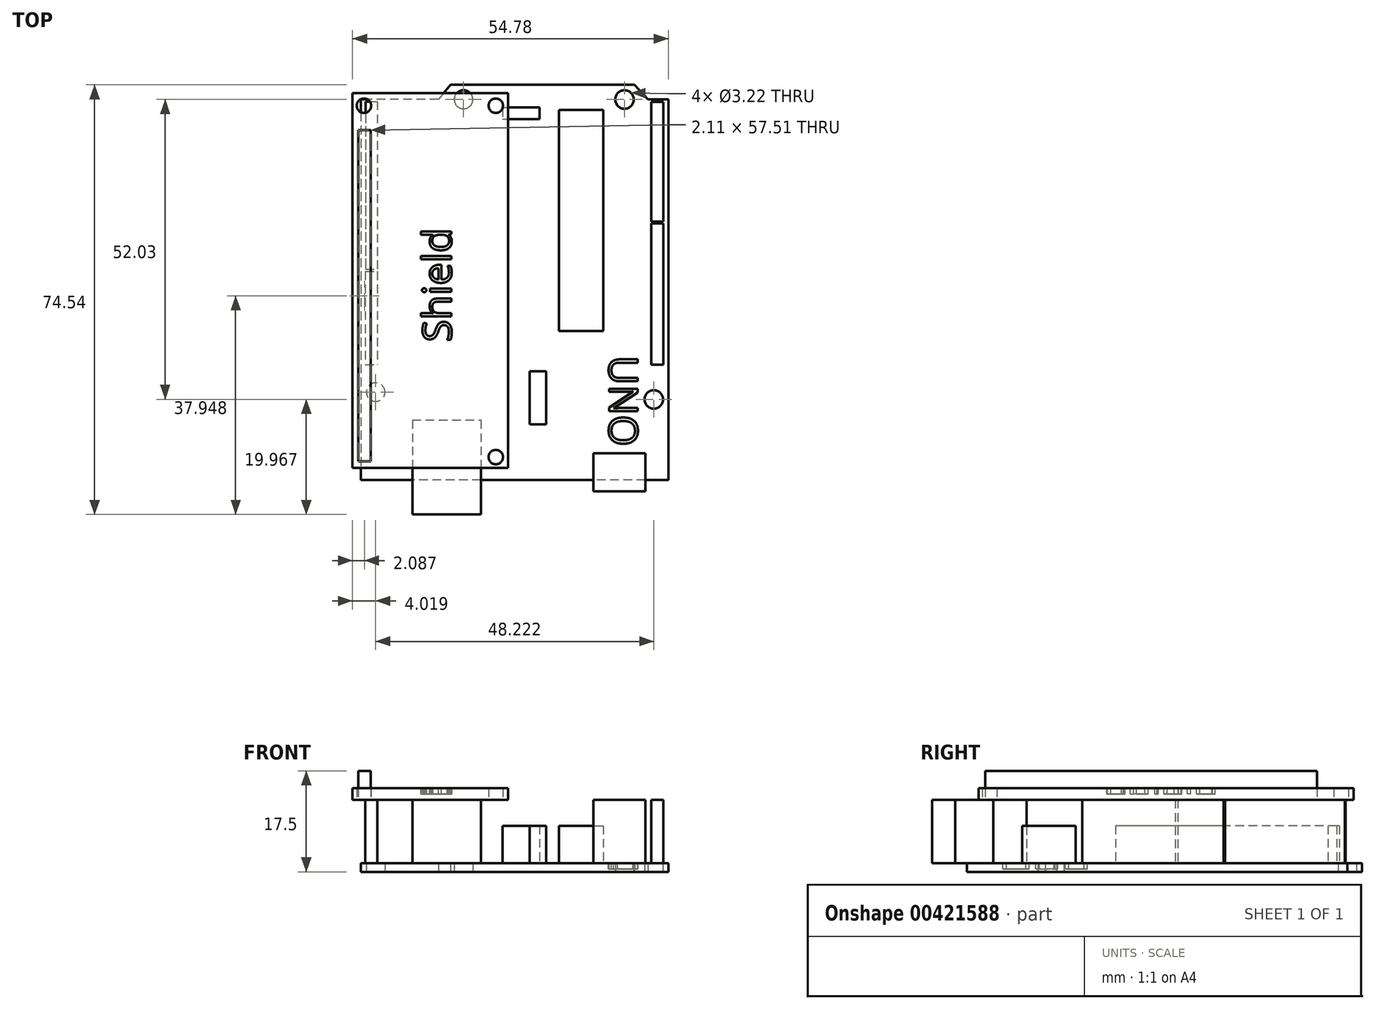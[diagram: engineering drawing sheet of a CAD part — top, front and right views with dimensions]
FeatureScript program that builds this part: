
annotation { "Feature Type Name" : "Feature", "Feature Type Description" : "" }
export const myFeature = defineFeature(function(context is Context, id is Id, definition is map)
    precondition{}
    {
        {
            var Q0;
            Q0=qCreatedBy(makeId("Top.planeOp"),FACE);
            var sketch = newSketch(context, id + "F0", { "sketchPlane" : qUnion([Q0])});
            skLineSegment(sketch, "E0.bottom", {"start": v(26.65, 33) * mm, "end": v(-26.65, 33) * mm});
            skLineSegment(sketch, "E0.top", {"start": v(26.65, -33) * mm, "end": v(-26.65, -33) * mm});
            skLineSegment(sketch, "E0.left", {"start": v(26.65, 33) * mm, "end": v(26.65, -33) * mm});
            skLineSegment(sketch, "E0.right", {"start": v(-26.65, 33) * mm, "end": v(-26.65, -33) * mm});
            skPoint(sketch, "E0.middle", {"position": v(0, 0) * mm});
            skLineSegment(sketch, "E1.bottom", {"start": v(-17.75, -22.62) * mm, "end": v(-5.85, -22.62) * mm});
            skLineSegment(sketch, "E1.top", {"start": v(-17.75, -39) * mm, "end": v(-5.85, -39) * mm});
            skLineSegment(sketch, "E1.left", {"start": v(-17.75, -22.62) * mm, "end": v(-17.75, -39) * mm});
            skLineSegment(sketch, "E1.right", {"start": v(-5.85, -22.62) * mm, "end": v(-5.85, -39) * mm});
            skLineSegment(sketch, "E2.bottom", {"start": v(7.67, 31.17) * mm, "end": v(15.35, 31.17) * mm});
            skLineSegment(sketch, "E2.top", {"start": v(7.67, -7.2) * mm, "end": v(15.35, -7.2) * mm});
            skLineSegment(sketch, "E2.left", {"start": v(7.67, 31.17) * mm, "end": v(7.67, -7.2) * mm});
            skLineSegment(sketch, "E2.right", {"start": v(15.35, 31.17) * mm, "end": v(15.35, -7.2) * mm});
            skLineSegment(sketch, "E3.bottom", {"start": v(2.6, -14.13) * mm, "end": v(5.43, -14.13) * mm});
            skLineSegment(sketch, "E3.top", {"start": v(2.6, -23.39) * mm, "end": v(5.43, -23.39) * mm});
            skLineSegment(sketch, "E3.left", {"start": v(2.6, -14.13) * mm, "end": v(2.6, -23.39) * mm});
            skLineSegment(sketch, "E3.right", {"start": v(5.43, -14.13) * mm, "end": v(5.43, -23.39) * mm});
            skLineSegment(sketch, "E4.bottom", {"start": v(-25.88, 32.67) * mm, "end": v(-23.85, 32.67) * mm});
            skLineSegment(sketch, "E4.top", {"start": v(-25.88, 3.57) * mm, "end": v(-23.85, 3.57) * mm});
            skLineSegment(sketch, "E4.left", {"start": v(-25.88, 32.67) * mm, "end": v(-25.88, 3.57) * mm});
            skLineSegment(sketch, "E4.right", {"start": v(-23.85, 32.67) * mm, "end": v(-23.85, 3.57) * mm});
            skLineSegment(sketch, "E5.bottom", {"start": v(-25.9, 3.18) * mm, "end": v(-23.82, 3.18) * mm});
            skLineSegment(sketch, "E5.top", {"start": v(-25.9, -13) * mm, "end": v(-23.82, -13) * mm});
            skLineSegment(sketch, "E5.left", {"start": v(-25.9, 3.18) * mm, "end": v(-25.9, -13) * mm});
            skLineSegment(sketch, "E5.right", {"start": v(-23.82, 3.18) * mm, "end": v(-23.82, -13) * mm});
            skLineSegment(sketch, "E6.bottom", {"start": v(25.78, 32.58) * mm, "end": v(23.65, 32.58) * mm});
            skLineSegment(sketch, "E6.top", {"start": v(25.78, 11.8) * mm, "end": v(23.65, 11.8) * mm});
            skLineSegment(sketch, "E6.left", {"start": v(23.65, 32.58) * mm, "end": v(23.65, 11.8) * mm});
            skLineSegment(sketch, "E7.bottom", {"start": v(25.75, 11.51) * mm, "end": v(23.66, 11.51) * mm});
            skLineSegment(sketch, "E7.top", {"start": v(25.75, -13) * mm, "end": v(23.66, -13) * mm});
            skLineSegment(sketch, "E7.left", {"start": v(25.75, 11.51) * mm, "end": v(25.75, -13) * mm});
            skLineSegment(sketch, "E7.right", {"start": v(23.66, 11.51) * mm, "end": v(23.66, -13) * mm});
            skLineSegment(sketch, "E8.bottom", {"start": v(-2.12, 31.63) * mm, "end": v(4.28, 31.63) * mm});
            skLineSegment(sketch, "E8.top", {"start": v(-2.12, 29.62) * mm, "end": v(4.28, 29.62) * mm});
            skLineSegment(sketch, "E8.left", {"start": v(-2.12, 31.63) * mm, "end": v(-2.12, 29.62) * mm});
            skLineSegment(sketch, "E8.right", {"start": v(4.28, 31.63) * mm, "end": v(4.28, 29.62) * mm});
            skText(sketch, "E9", { "text": "UNO", "fontName": "OpenSans-Regular.ttf"});
            skCircle(sketch, "E10", {"center": v(19.03, 33) * mm, "radius": 1.6 * mm});
            skCircle(sketch, "E11", {"center": v(-8.88, 33) * mm, "radius": 1.6 * mm});
            skLineSegment(sketch, "E12", {"start": v(-11.15, 35.54) * mm, "end": v(20.74, 35.54) * mm});
            skLineSegment(sketch, "E13", {"start": v(20.74, 35.54) * mm, "end": v(23.07, 33) * mm});
            skCircle(sketch, "E14", {"center": v(24.11, -19.03) * mm, "radius": 1.6 * mm});
            skLineSegment(sketch, "E15", {"start": v(25.78, 11.8) * mm, "end": v(25.78, 32.58) * mm});
            skCircle(sketch, "E16", {"center": v(-24.11, -17.76) * mm, "radius": 1.6 * mm});
            skLineSegment(sketch, "E17", {"start": v(-11.15, 35.54) * mm, "end": v(-13.22, 33) * mm});
            skLineSegment(sketch, "E18", {"start": v(13.65, -28.4) * mm, "end": v(13.65, -35) * mm});
            skLineSegment(sketch, "E19", {"start": v(13.65, -35) * mm, "end": v(22.65, -35) * mm});
            skLineSegment(sketch, "E20", {"start": v(22.65, -35) * mm, "end": v(22.65, -28.4) * mm});
            skLineSegment(sketch, "E21", {"start": v(22.65, -28.4) * mm, "end": v(13.65, -28.4) * mm});
            const initialGuessF0  = {"E9": [0.01473, -0.00947, 0, -1, 0.005]};
            skSetInitialGuess(sketch, initialGuessF0);
            skSolve(sketch);
        }
        {
            var Q0;
            Q0=makeQuery(id+"F0.imprint","IMPRINT",FACE,{"disambiguationData":[TD([[makeQuery(id+"F0.imprint","IMPRINT",EDGE,{"derivedFrom":sQuery(id+"F0.wireOp",EDGE,"E0.bottom")}),1.0]])]});
            var Q1;
            Q1=makeQuery(id+"F0.imprint","IMPRINT",FACE,{"disambiguationData":[TD([[makeQuery(id+"F0.imprint","IMPRINT",EDGE,{"derivedFrom":sQuery(id+"F0.wireOp",EDGE,"E9.sketch_text.stroke-37")}),1.0]])]});
            var Q2;
            Q2=makeQuery(id+"F0.imprint","IMPRINT",FACE,{"disambiguationData":[TD([[makeQuery(id+"F0.imprint","IMPRINT",EDGE,{"derivedFrom":sQuery(id+"F0.wireOp",EDGE,"E9.sketch_text.stroke-0")}),-1.0]])]});
            var Q3;
            Q3=makeQuery(id+"F0.imprint","IMPRINT",FACE,{"disambiguationData":[TD([[makeQuery(id+"F0.imprint","IMPRINT",EDGE,{"derivedFrom":sQuery(id+"F0.wireOp",EDGE,"E9.sketch_text.stroke-14")}),-1.0]])]});
            var Q4;
            Q4=makeQuery(id+"F0.imprint","IMPRINT",FACE,{"disambiguationData":[TD([[makeQuery(id+"F0.imprint","IMPRINT",EDGE,{"derivedFrom":sQuery(id+"F0.wireOp",EDGE,"E9.sketch_text.stroke-29")}),-1.0]])]});
            var Q5;
            Q5=makeQuery(id+"F0.imprint","IMPRINT",FACE,{"disambiguationData":[TD([[makeQuery(id+"F0.imprint","IMPRINT",EDGE,{"derivedFrom":sQuery(id+"F0.wireOp",EDGE,"E12")}),-1.0]])]});
            extrude(context, id + "F1", {"entities" : qUnion([Q0, Q1, Q2, Q3, Q4, Q5]), "depth" : 1.5 * mm, "offsetDistance" : 25 * mm});
        }
        {
            var Q0;
            Q0=makeQuery(id+"F0.imprint","IMPRINT",FACE,{"disambiguationData":[TD([[makeQuery(id+"F0.imprint","IMPRINT",EDGE,{"derivedFrom":sQuery(id+"F0.wireOp",EDGE,"E4.bottom")}),-1.0]])]});
            var Q1;
            Q1=makeQuery(id+"F0.imprint","IMPRINT",FACE,{"disambiguationData":[TD([[makeQuery(id+"F0.imprint","IMPRINT",EDGE,{"derivedFrom":sQuery(id+"F0.wireOp",EDGE,"E6.bottom")}),1.0]])]});
            var Q2;
            Q2=makeQuery(id+"F0.imprint","IMPRINT",FACE,{"disambiguationData":[TD([[makeQuery(id+"F0.imprint","IMPRINT",EDGE,{"derivedFrom":sQuery(id+"F0.wireOp",EDGE,"E7.bottom")}),1.0]])]});
            var Q3;
            Q3=makeQuery(id+"F0.imprint","IMPRINT",FACE,{"disambiguationData":[TD([[makeQuery(id+"F0.imprint","IMPRINT",EDGE,{"derivedFrom":sQuery(id+"F0.wireOp",EDGE,"E5.bottom")}),-1.0]])]});
            var Q4;
            {var subQ5=sQuery(id+"F0.wireOp",EDGE,"E1.top");Q4=makeQuery(id+"F0.imprint","IMPRINT",FACE,{"disambiguationData":[TD([[makeQuery(id+"F0.imprint","IMPRINT",EDGE,{"derivedFrom":subQ5}),1.0]])]});}
            var Q5;
            {var subQ5=sQuery(id+"F0.wireOp",EDGE,"E1.bottom");Q5=makeQuery(id+"F0.imprint","IMPRINT",FACE,{"disambiguationData":[TD([[makeQuery(id+"F0.imprint","IMPRINT",EDGE,{"derivedFrom":subQ5}),-1.0]])]});}
            var Q6;
            {var subQ5=sQuery(id+"F0.wireOp",EDGE,"0UXD3os9-Lv6w-TNBq-ahMY-INUZyBISBa7V.top");Q6=makeQuery(id+"F0.imprint","IMPRINT",FACE,{"disambiguationData":[TD([[makeQuery(id+"F0.imprint","IMPRINT",EDGE,{"derivedFrom":subQ5}),-1.0]])]});}
            var Q7;
            {var subQ5=sQuery(id+"F0.wireOp",EDGE,"0UXD3os9-Lv6w-TNBq-ahMY-INUZyBISBa7V.bottom");Q7=makeQuery(id+"F0.imprint","IMPRINT",FACE,{"disambiguationData":[TD([[makeQuery(id+"F0.imprint","IMPRINT",EDGE,{"derivedFrom":subQ5}),1.0]])]});}
            var Q8;
            {var subQ5=sQuery(id+"F0.wireOp",EDGE,"E21");Q8=makeQuery(id+"F0.imprint","IMPRINT",FACE,{"disambiguationData":[TD([[makeQuery(id+"F0.imprint","IMPRINT",EDGE,{"derivedFrom":subQ5}),1.0]])]});}
            var Q9;
            {var subQ5=sQuery(id+"F0.wireOp",EDGE,"E19");Q9=makeQuery(id+"F0.imprint","IMPRINT",FACE,{"disambiguationData":[TD([[makeQuery(id+"F0.imprint","IMPRINT",EDGE,{"derivedFrom":subQ5}),1.0]])]});}
            extrude(context, id + "F2", {"entities" : qUnion([Q0, Q1, Q2, Q3, Q4, Q5, Q6, Q7, Q8, Q9]), "operationType" : NewBodyOperationType.ADD, "depth" : 12.5 * mm, "offsetDistance" : 25 * mm});
        }
        {
            var Q0;
            Q0=makeQuery(id+"F0.imprint","IMPRINT",FACE,{"disambiguationData":[TD([[makeQuery(id+"F0.imprint","IMPRINT",EDGE,{"derivedFrom":sQuery(id+"F0.wireOp",EDGE,"E2.bottom")}),-1.0]])]});
            var Q1;
            Q1=makeQuery(id+"F0.imprint","IMPRINT",FACE,{"disambiguationData":[TD([[makeQuery(id+"F0.imprint","IMPRINT",EDGE,{"derivedFrom":sQuery(id+"F0.wireOp",EDGE,"E8.bottom")}),-1.0]])]});
            var Q2;
            Q2=makeQuery(id+"F0.imprint","IMPRINT",FACE,{"disambiguationData":[TD([[makeQuery(id+"F0.imprint","IMPRINT",EDGE,{"derivedFrom":sQuery(id+"F0.wireOp",EDGE,"E3.bottom")}),-1.0]])]});
            extrude(context, id + "F3", {"entities" : qUnion([Q0, Q1, Q2]), "operationType" : NewBodyOperationType.ADD, "depth" : 8 * mm, "offsetDistance" : 25 * mm});
        }
        {
            var Q0;
            Q0=makeQuery(id+"F2.opExtrude","CAP_FACE",FACE,{"disambiguationData":[OSD([sQuery(id+"F0.wireOp",EDGE,"E5.bottom"),sQuery(id+"F0.wireOp",EDGE,"E5.top"),sQuery(id+"F0.wireOp",EDGE,"E5.left"),sQuery(id+"F0.wireOp",EDGE,"E5.right")])],"isStart":false});
            cPlane(context, id + "F4", {"entities" : qUnion([Q0]), "cplaneType" : CPlaneType.OFFSET, "offset" : 0 * mm, "width" : 150 * mm, "height" : 150 * mm});
        }
        {
            var Q0;
            Q0=qCreatedBy(id+"F4.planeOp",FACE);
            var sketch = newSketch(context, id + "F5", { "sketchPlane" : qUnion([Q0])});
            skLineSegment(sketch, "E22.bottom", {"start": v(-28.13, -30.92) * mm, "end": v(-1.13, -30.92) * mm});
            skLineSegment(sketch, "E22.top", {"start": v(-28.13, 34.08) * mm, "end": v(-1.13, 34.08) * mm});
            skLineSegment(sketch, "E22.left", {"start": v(-28.13, -30.92) * mm, "end": v(-28.13, 34.08) * mm});
            skLineSegment(sketch, "E22.right", {"start": v(-1.13, -30.92) * mm, "end": v(-1.13, 34.08) * mm});
            skLineSegment(sketch, "E23.bottom", {"start": v(-27.1, 27.7) * mm, "end": v(-24.99, 27.7) * mm});
            skLineSegment(sketch, "E23.top", {"start": v(-27.1, -29.8) * mm, "end": v(-24.99, -29.8) * mm});
            skLineSegment(sketch, "E23.left", {"start": v(-27.1, 27.7) * mm, "end": v(-27.1, -29.8) * mm});
            skLineSegment(sketch, "E23.right", {"start": v(-24.99, 27.7) * mm, "end": v(-24.99, -29.8) * mm});
            skCircle(sketch, "E24", {"center": v(-26.14, 31.91) * mm, "radius": 1.25 * mm});
            skCircle(sketch, "E25", {"center": v(-3.28, 31.91) * mm, "radius": 1.25 * mm});
            skCircle(sketch, "E26", {"center": v(-3.28, -29.05) * mm, "radius": 1.25 * mm});
            skSolve(sketch);
        }
        {
            var Q0;
            Q0 = qSketchRegion(id + "F5", true);
            extrude(context, id + "F6", {"entities" : qUnion([Q0]), "depth" : 2 * mm, "offsetDistance" : 25 * mm});
        }
        {
            var Q0;
            Q0=makeQuery(id+"F5.imprint","IMPRINT",FACE,{"disambiguationData":[TD([[makeQuery(id+"F5.imprint","IMPRINT",EDGE,{"derivedFrom":sQuery(id+"F5.wireOp",EDGE,"E23.bottom")}),-1.0]])]});
            extrude(context, id + "F7", {"entities" : qUnion([Q0]), "depth" : 5 * mm, "offsetDistance" : 25 * mm});
        }
        {
            var Q0;
            Q0=makeQuery(id+"F1.opExtrude","CAP_FACE",FACE,{"disambiguationData":[OSD([sQuery(id+"F0.wireOp",EDGE,"E0.bottom"),sQuery(id+"F0.wireOp",EDGE,"E0.top"),sQuery(id+"F0.wireOp",EDGE,"E0.left"),sQuery(id+"F0.wireOp",EDGE,"E0.right"),sQuery(id+"F0.wireOp",EDGE,"E1.bottom"),sQuery(id+"F0.wireOp",EDGE,"E1.left"),sQuery(id+"F0.wireOp",EDGE,"E1.right"),sQuery(id+"F0.wireOp",EDGE,"0UXD3os9-Lv6w-TNBq-ahMY-INUZyBISBa7V.top"),sQuery(id+"F0.wireOp",EDGE,"0UXD3os9-Lv6w-TNBq-ahMY-INUZyBISBa7V.left"),sQuery(id+"F0.wireOp",EDGE,"0UXD3os9-Lv6w-TNBq-ahMY-INUZyBISBa7V.right"),sQuery(id+"F0.wireOp",EDGE,"E2.bottom"),sQuery(id+"F0.wireOp",EDGE,"E2.top"),sQuery(id+"F0.wireOp",EDGE,"E2.left"),sQuery(id+"F0.wireOp",EDGE,"E2.right"),sQuery(id+"F0.wireOp",EDGE,"E3.bottom"),sQuery(id+"F0.wireOp",EDGE,"E3.top"),sQuery(id+"F0.wireOp",EDGE,"E3.left"),sQuery(id+"F0.wireOp",EDGE,"E3.right"),sQuery(id+"F0.wireOp",EDGE,"E4.bottom"),sQuery(id+"F0.wireOp",EDGE,"E4.top"),sQuery(id+"F0.wireOp",EDGE,"E4.left"),sQuery(id+"F0.wireOp",EDGE,"E4.right"),sQuery(id+"F0.wireOp",EDGE,"E5.bottom"),sQuery(id+"F0.wireOp",EDGE,"E5.top"),sQuery(id+"F0.wireOp",EDGE,"E5.left"),sQuery(id+"F0.wireOp",EDGE,"E5.right"),sQuery(id+"F0.wireOp",EDGE,"E6.bottom"),sQuery(id+"F0.wireOp",EDGE,"E6.top"),sQuery(id+"F0.wireOp",EDGE,"E6.left"),sQuery(id+"F0.wireOp",EDGE,"E6.right"),sQuery(id+"F0.wireOp",EDGE,"E7.bottom"),sQuery(id+"F0.wireOp",EDGE,"E7.top"),sQuery(id+"F0.wireOp",EDGE,"E7.left"),sQuery(id+"F0.wireOp",EDGE,"E7.right"),sQuery(id+"F0.wireOp",EDGE,"E8.bottom"),sQuery(id+"F0.wireOp",EDGE,"E8.top"),sQuery(id+"F0.wireOp",EDGE,"E8.left"),sQuery(id+"F0.wireOp",EDGE,"E8.right")])],"isStart":false});
            cPlane(context, id + "F8", {"entities" : qUnion([Q0]), "cplaneType" : CPlaneType.OFFSET, "offset" : 0 * mm, "width" : 150 * mm, "height" : 150 * mm});
        }
        {
            var Q0;
            Q0=qCreatedBy(id+"F8.planeOp",FACE);
            var sketch = newSketch(context, id + "F9", { "sketchPlane" : qUnion([Q0])});
            skText(sketch, "E27", { "text": "UNO", "fontName": "OpenSans-Regular.ttf"});
            const initialGuessF9  = {"E27": [0.01634, -0.01146, 0, -1, 0.005]};
            skSetInitialGuess(sketch, initialGuessF9);
            skSolve(sketch);
        }
        {
            var Q0;
            Q0=makeQuery(id+"F9.imprint","IMPRINT",FACE,{"disambiguationData":[TD([[makeQuery(id+"F9.imprint","IMPRINT",EDGE,{"derivedFrom":sQuery(id+"F9.wireOp",EDGE,"E27.sketch_text.stroke-0")}),-1.0]])]});
            var Q1;
            Q1 = qSketchRegion(id + "F9", true);
            var Q2;
            Q2=makeQuery(id+"F9.imprint","IMPRINT",FACE,{"disambiguationData":[TD([[makeQuery(id+"F9.imprint","IMPRINT",EDGE,{"derivedFrom":sQuery(id+"F9.wireOp",EDGE,"E27.sketch_text.stroke-29")}),-1.0]])]});
            extrude(context, id + "F10", {"entities" : qUnion([Q0, Q1, Q2]), "operationType" : NewBodyOperationType.REMOVE, "oppositeDirection" : true, "depth" : 1 * mm, "offsetDistance" : 25 * mm});
        }
        {
            var Q0;
            Q0=makeQuery(id+"F6.opExtrude","CAP_FACE",FACE,{"disambiguationData":[OSD([sQuery(id+"F5.wireOp",EDGE,"E22.bottom"),sQuery(id+"F5.wireOp",EDGE,"E22.top"),sQuery(id+"F5.wireOp",EDGE,"E22.left"),sQuery(id+"F5.wireOp",EDGE,"E22.right"),sQuery(id+"F5.wireOp",EDGE,"E23.bottom"),sQuery(id+"F5.wireOp",EDGE,"E23.top"),sQuery(id+"F5.wireOp",EDGE,"E23.left"),sQuery(id+"F5.wireOp",EDGE,"E23.right")])],"isStart":false});
            var sketch = newSketch(context, id + "F11", { "sketchPlane" : qUnion([Q0])});
            skText(sketch, "E28", { "text": "Shield", "fontName": "OpenSans-Regular.ttf"});
            const initialGuessF11  = {"E28": [-0.01098, -0.00905, 0, 1, 0.005]};
            skSetInitialGuess(sketch, initialGuessF11);
            skSolve(sketch);
        }
        {
            var Q0;
            Q0 = qSketchRegion(id + "F11", true);
            extrude(context, id + "F12", {"entities" : qUnion([Q0]), "operationType" : NewBodyOperationType.REMOVE, "oppositeDirection" : true, "depth" : 1 * mm, "offsetDistance" : 25 * mm});
        }
        {
            var Q0;
            {var subQ5=sQuery(id+"F0.wireOp",EDGE,"E19");Q0=makeQuery(id+"F0.imprint","IMPRINT",FACE,{"disambiguationData":[TD([[makeQuery(id+"F0.imprint","IMPRINT",EDGE,{"derivedFrom":subQ5}),1.0]])]});}
            var Q1;
            {var subQ5=sQuery(id+"F0.wireOp",EDGE,"E1.top");Q1=makeQuery(id+"F0.imprint","IMPRINT",FACE,{"disambiguationData":[TD([[makeQuery(id+"F0.imprint","IMPRINT",EDGE,{"derivedFrom":subQ5}),1.0]])]});}
            extrude(context, id + "F13", {"entities" : qUnion([Q0, Q1]), "operationType" : NewBodyOperationType.REMOVE, "depth" : 1.5 * mm, "offsetDistance" : 25 * mm});
        }
    });
